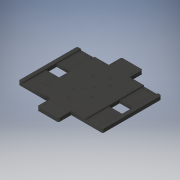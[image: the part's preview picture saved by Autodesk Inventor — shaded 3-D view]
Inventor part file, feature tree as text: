
AUTODESK INVENTOR PART (.ipt)
format: ipt  version: 2017 (Build 210142000, 142)  size: 488,960 bytes
history: native  units: in
note: dims shown in document units (in); Inventor stores cm internally (conversion verified against a paired STEP export)
features: extrude x10, sketch x10, projected_geometry x10, fillet x1
ambient origin geometry x8: Origin, YZ Plane, XZ Plane, XY Plane, X Axis, Y Axis, Z Axis, Center Point
bodies: Solid1 (feature_tree)
feature tree (31):
  extrude  "Extrusion1"  Depth=9.0in
  extrude  "Extrusion2"  Depth=1.118in
  extrude  "Extrusion3"  Depth=0.25in
  extrude  "Extrusion4"  TaperAngle=0.0deg  [1 undecoded]
  extrude  "Extrusion5"  Depth=0.375in
  extrude  "Extrusion7"  Depth=0.125in
  extrude  "ardMount"  Depth=0.125in TaperAngle=0.0deg
  extrude  "piMount"  Depth=0.125in TaperAngle=0.0deg
  extrude  "sabertoothMount"  Depth=3.0in
  extrude  "Extrusion11"  Depth=0.125in TaperAngle=0.0deg
  fillet  "Fillet1"  Radius=1.368in
  sketch  "Sketch1"  dims[d0=9.0in d1=9.0in]
  sketch  "Sketch2"  dims[d2=2.3622in d3=1.118in]
  projected_geometry  "Projected Loop1"
  sketch  "Sketch3"  dims[d4=0.375in d5=0.0in d6=0.25in]
  projected_geometry  "Projected Loop2"
  projected_geometry  "Projected Loop3"
  projected_geometry  "Projected Loop4"
  projected_geometry  "Projected Loop5"
  sketch  "Sketch4"  dims[d7=0.375in d8=0.0in]
  sketch  "Sketch5"  dims[d9=1.5in d10=0.375in]
  sketch  "Sketch7"  dims[d11=0.125in d12=0.5827in]
  projected_geometry  "Projected Loop7"
  sketch  "Sketch8"  dims[d13=0.125in d14=0.0312in d15=0.0in]
  projected_geometry  "Projected Loop8"
  sketch  "Sketch9"  dims[d16=0.125in d17=0.0in d18=0.125in d19=0.0in]
  projected_geometry  "Projected Loop9"
  sketch  "Sketch10"  dims[d20=1.5in d21=3.0in]
  projected_geometry  "Projected Loop10"
  sketch  "Sketch11"  dims[d22=0.125in d23=0.125in d24=0.0in d30=1.368in d31=1.0in d32=0.0in d33=0.209in d34=3.543in d35=0.63in d36=0.209in d37=0.571in d38=3.799in d39=0.125in d40=0.125in d41=0.125in d42=0.125in d43=1.0in d44=0.0in d45=0.184in d46=0.93in d47=3.21in d48=0.125in d49=0.125in d50=1.0in d51=0.0in d52=2.026in d53=2.859in d54=1.121in d55=4.275in d56=2.026in d57=2.859in d58=1.121in d59=4.275in d60=0.125in d61=0.125in d62=0.125in d63=0.125in d64=0.125in d65=0.125in d66=0.125in d67=0.125in d68=1.0in d69=0.0in d70=1.125in d71=1.0in d72=0.0in d73=0.125in]
  projected_geometry  "Projected Loop11"
note: 1 required parameter value undecoded (feature->parameter linkage not recoverable at this tier; creation-order binding heuristic only, values carry confidence <= 0.55)
